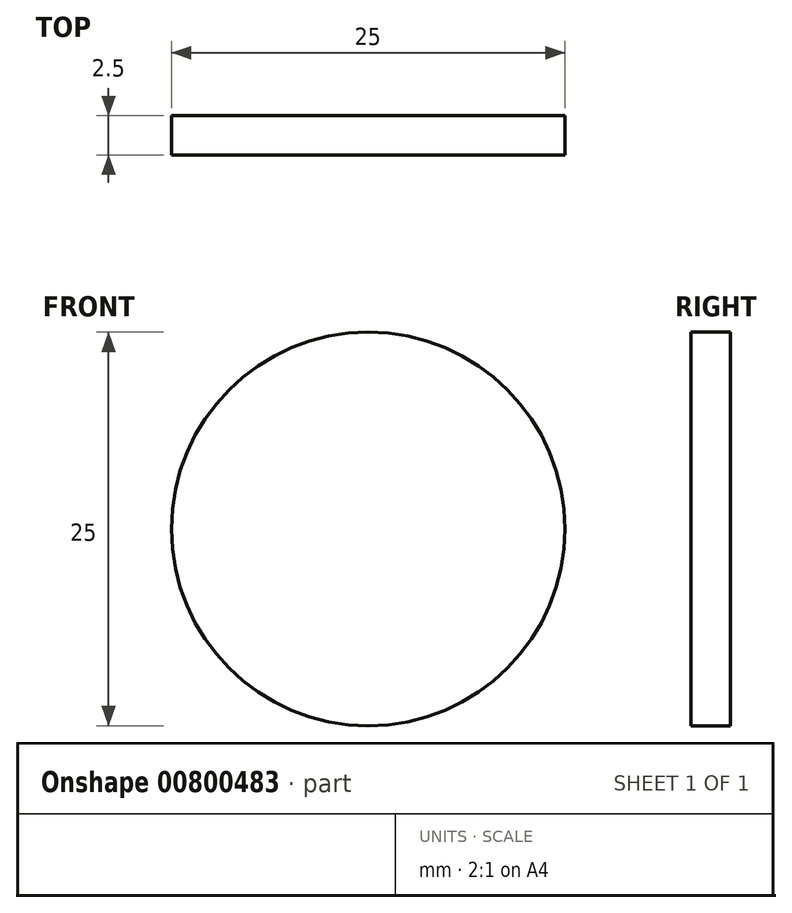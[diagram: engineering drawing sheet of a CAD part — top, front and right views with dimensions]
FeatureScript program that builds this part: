
annotation { "Feature Type Name" : "Feature", "Feature Type Description" : "" }
export const myFeature = defineFeature(function(context is Context, id is Id, definition is map)
    precondition{}
    {
        {
            var Q0;
            Q0=qCreatedBy(makeId("Front.planeOp"),FACE);
            var sketch = newSketch(context, id + "F0", { "sketchPlane" : qUnion([Q0])});
            skCircle(sketch, "E0", {"center": v(0, 0) * mm, "radius": 12.5 * mm});
            skSolve(sketch);
        }
        {
            var Q0;
            Q0=makeQuery(id+"F0.imprint","IMPRINT",FACE,{"disambiguationData":[TD([[makeQuery(id+"F0.imprint","IMPRINT",EDGE,{"derivedFrom":sQuery(id+"F0.wireOp",EDGE,"E0")}),1.0]])]});
            extrude(context, id + "F1", {"entities" : qUnion([Q0]), "depth" : 2.5 * mm, "offsetDistance" : 25 * mm});
        }
    });
